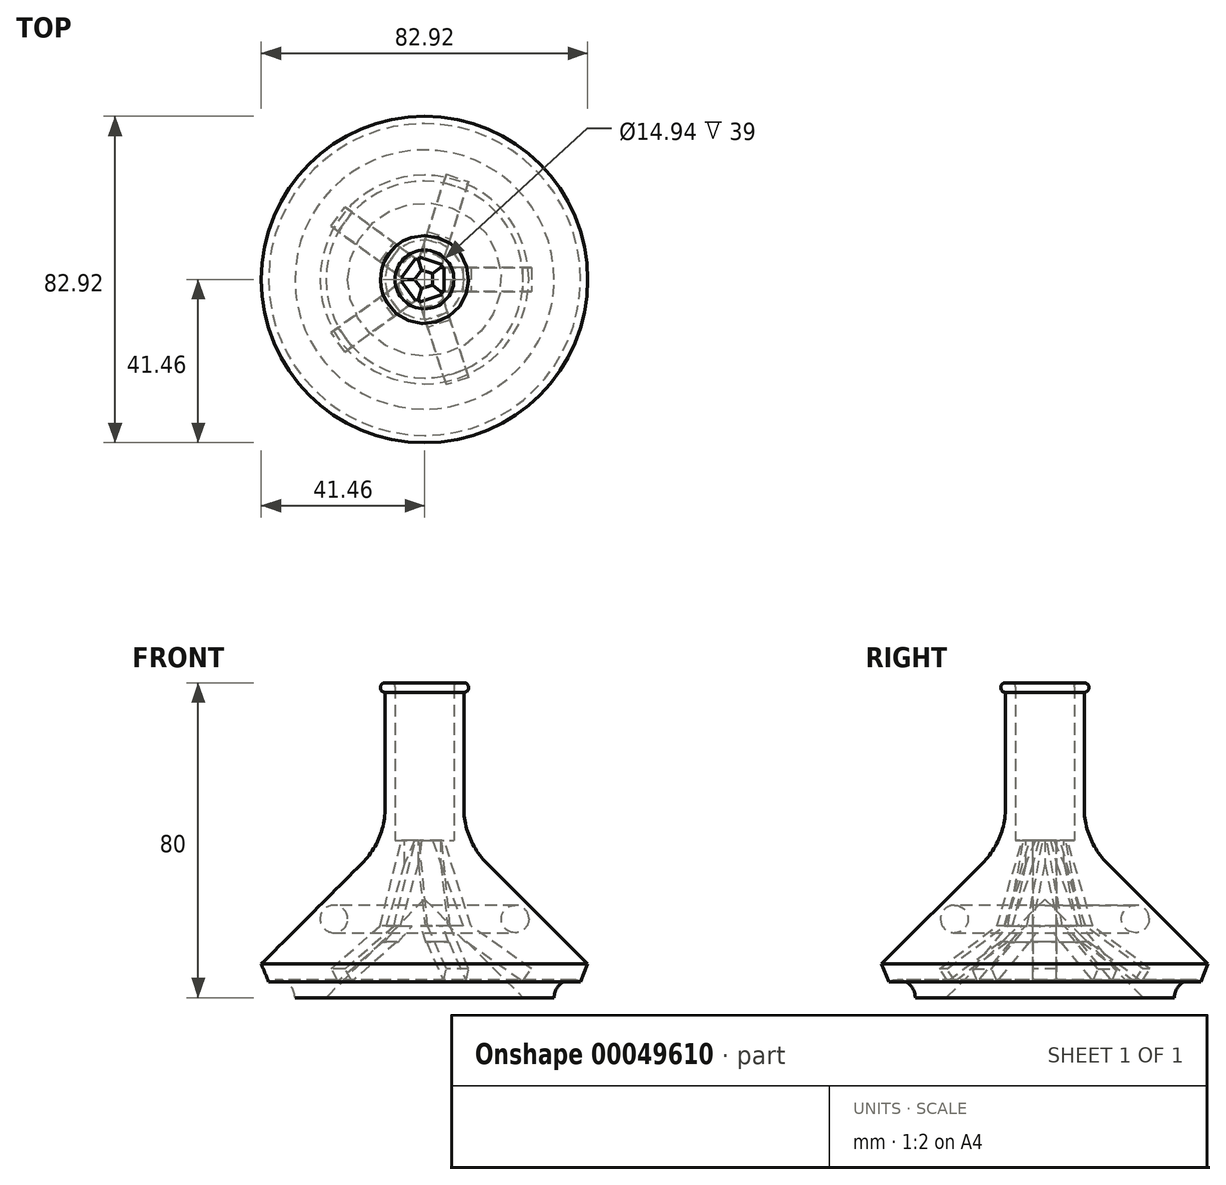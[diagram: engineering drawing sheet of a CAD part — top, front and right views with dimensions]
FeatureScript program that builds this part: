
annotation { "Feature Type Name" : "Feature", "Feature Type Description" : "" }
export const myFeature = defineFeature(function(context is Context, id is Id, definition is map)
    precondition{}
    {
        {
            var Q0;
            Q0=qCreatedBy(makeId("Front.planeOp"),FACE);
            var sketch = newSketch(context, id + "F0", { "sketchPlane" : qUnion([Q0])});
            skLineSegment(sketch, "E0", {"start": v(0, 0) * mm, "end": v(0, 80) * mm, "construction": true});
            skLineSegment(sketch, "E1", {"start": v(0, 80) * mm, "end": v(10, 80) * mm, "construction": true});
            skLineSegment(sketch, "E2", {"start": v(10, 80) * mm, "end": v(10, 40) * mm});
            skLineSegment(sketch, "E3", {"start": v(10, 40) * mm, "end": v(50, 0) * mm});
            skLineSegment(sketch, "E4", {"start": v(50, 0) * mm, "end": v(0, 0) * mm, "construction": true});
            skLineSegment(sketch, "E5", {"start": v(10, 80) * mm, "end": v(7.47, 80) * mm});
            skLineSegment(sketch, "E6", {"start": v(7.47, 80) * mm, "end": v(7.47, 40) * mm});
            skLineSegment(sketch, "E7", {"start": v(7.47, 40) * mm, "end": v(0, 40) * mm});
            skLineSegment(sketch, "E8", {"start": v(0, 40) * mm, "end": v(0, 25) * mm});
            skLineSegment(sketch, "E9", {"start": v(25, 0) * mm, "end": v(50, 0) * mm, "construction": true});
            skArc(sketch, "E10", {"start": v(42.08, 0) * mm, "mid": v(37.5, 4.58) * mm, "end": v(32.92, 0) * mm});
            skLineSegment(sketch, "E11", {"start": v(25, 0) * mm, "end": v(32.92, 0) * mm});
            skLineSegment(sketch, "E12", {"start": v(42.08, 0) * mm, "end": v(50, 0) * mm});
            skArc(sketch, "E13", {"start": v(10, 77.59) * mm, "mid": v(11.2, 78.8) * mm, "end": v(10, 80) * mm});
            skLineSegment(sketch, "E14", {"start": v(0, 25) * mm, "end": v(25, 0) * mm});
            skLineSegment(sketch, "E15", {"start": v(30, 20) * mm, "end": v(23, 20) * mm, "construction": true});
            skCircle(sketch, "E16", {"center": v(23, 20) * mm, "radius": 3.5 * mm});
            skSolve(sketch);
        }
        {
            var Q0;
            Q0=qSketchRegion(id+"F0",true);
            var Q1;
            Q1=sQuery(id+"F0.wireOp",EDGE,"E0");
            revolve(context, id + "F1", {"entities" : qUnion([Q0]), "axis" : qUnion([Q1]), "revolveType" : RevolveType.SYMMETRIC, "angle" : 72 * degree});
        }
        {
            var Q0;
            Q0=qCreatedBy(makeId("Front.planeOp"),FACE);
            var sketch = newSketch(context, id + "F2", { "sketchPlane" : qUnion([Q0])});
            skPoint(sketch, "E17.0", {"position": v(0, 40) * mm});
            skLineSegment(sketch, "E18", {"start": v(5.99, 44.01) * mm, "end": v(50, 0) * mm, "construction": true});
            skLineSegment(sketch, "E19", {"start": v(10, 80) * mm, "end": v(10, 40) * mm, "construction": true});
            skLineSegment(sketch, "E20", {"start": v(0, 40) * mm, "end": v(2, 40) * mm, "construction": true});
            skLineSegment(sketch, "E21", {"start": v(2, 40) * mm, "end": v(5, 40) * mm});
            skLineSegment(sketch, "E22", {"start": v(28, 22) * mm, "end": v(27.29, 21.3) * mm, "construction": true});
            skLineSegment(sketch, "E23", {"start": v(27.29, 21.3) * mm, "end": v(5, 40) * mm, "construction": true});
            skLineSegment(sketch, "E24", {"start": v(27.29, 21.3) * mm, "end": v(26, 19.77) * mm, "construction": true});
            skLineSegment(sketch, "E25", {"start": v(26, 19.77) * mm, "end": v(2, 40) * mm, "construction": true});
            skLineSegment(sketch, "E26", {"start": v(26.64, 20.53) * mm, "end": v(29.7, 17.96) * mm, "construction": true});
            skLineSegment(sketch, "E27", {"start": v(29.7, 17.96) * mm, "end": v(33.45, 16.55) * mm, "construction": true});
            skLineSegment(sketch, "E28", {"start": v(33.45, 16.55) * mm, "end": v(28, 22) * mm, "construction": true});
            skLineSegment(sketch, "E29", {"start": v(26, 19.77) * mm, "end": v(26, 0) * mm, "construction": true});
            skLineSegment(sketch, "E30", {"start": v(26, 0) * mm, "end": v(29.7, 0) * mm, "construction": true});
            skLineSegment(sketch, "E31", {"start": v(29.7, 0) * mm, "end": v(29.7, 17.96) * mm, "construction": true});
            skLineSegment(sketch, "E32", {"start": v(0.24, 24.76) * mm, "end": v(21.38, 3.62) * mm, "construction": true});
            skLineSegment(sketch, "E33", {"start": v(2, 40) * mm, "end": v(9.81, 18.19) * mm});
            skLineSegment(sketch, "E34", {"start": v(6.81, 18.19) * mm, "end": v(4.63, 18.19) * mm});
            skLineSegment(sketch, "E35", {"start": v(4.63, 18.19) * mm, "end": v(9.72, 13.1) * mm});
            skLineSegment(sketch, "E36", {"start": v(9.72, 13.1) * mm, "end": v(10.81, 14.19) * mm});
            skLineSegment(sketch, "E37", {"start": v(10.81, 14.19) * mm, "end": v(24.92, 4.18) * mm});
            skLineSegment(sketch, "E38", {"start": v(24.92, 4.18) * mm, "end": v(27.14, 7.3) * mm});
            skLineSegment(sketch, "E39", {"start": v(27.14, 7.3) * mm, "end": v(11.81, 18.19) * mm});
            skLineSegment(sketch, "E40", {"start": v(11.81, 18.19) * mm, "end": v(5, 40) * mm});
            skLineSegment(sketch, "E41", {"start": v(11.81, 18.19) * mm, "end": v(9.81, 18.19) * mm, "construction": true});
            skLineSegment(sketch, "E42", {"start": v(10.81, 18.19) * mm, "end": v(10.81, 14.19) * mm, "construction": true});
            skLineSegment(sketch, "E43", {"start": v(6.81, 18.19) * mm, "end": v(9.81, 18.19) * mm});
            skSolve(sketch);
        }
        {
            var Q0;
            Q0=qSketchRegion(id+"F2",true);
            extrude(context, id + "F3", {"entities" : qUnion([Q0]), "operationType" : NewBodyOperationType.REMOVE, "endBound" : BoundingType.SYMMETRIC, "oppositeDirection" : true, "depth" : 6 * mm});
        }
        {
            var Q0;
            Q0=makeQuery(id+"F1.opRevolve","SWEPT_BODY",BODY,{"disambiguationData":[OSD([sQuery(id+"F0.wireOp",EDGE,"E2"),sQuery(id+"F0.wireOp",EDGE,"E3"),sQuery(id+"F0.wireOp",EDGE,"E5"),sQuery(id+"F0.wireOp",EDGE,"E6"),sQuery(id+"F0.wireOp",EDGE,"E7"),sQuery(id+"F0.wireOp",EDGE,"93deaf08-34c0-4183-b7e3-c0240623c559"),sQuery(id+"F0.wireOp",EDGE,"E8"),sQuery(id+"F0.wireOp",EDGE,"E10"),sQuery(id+"F0.wireOp",EDGE,"E11"),sQuery(id+"F0.wireOp",EDGE,"E12")])]});
            var Q1;
            Q1=makeQuery(id+"F1.opRevolve","CAP_EDGE",EDGE,{"disambiguationData":[OSD([sQuery(id+"F0.wireOp",EDGE,"E8")])],"isStart":true});
            circularPattern(context, id + "F4", {"operationType" : NewBodyOperationType.ADD, "entities" : qUnion([Q0]), "axis" : qUnion([Q1]), "angle" : 72 * degree, "instanceCount" : 5});
        }
        {
            var Q0;
            {var subQ0=makeQuery(id+"F1.opRevolve","SWEPT_FACE",FACE,{"disambiguationData":[OSD([sQuery(id+"F0.wireOp",EDGE,"E5")])]});Q0=makeQuery(id+"F4.boolean.opBoolean","MERGE",FACE,{"derivedFrom":[subQ0,makeQuery(id+"F4.opPattern","COPY",FACE,{"derivedFrom":subQ0,"instanceName":"1"}),makeQuery(id+"F4.opPattern","COPY",FACE,{"derivedFrom":subQ0,"instanceName":"2"}),makeQuery(id+"F4.opPattern","COPY",FACE,{"derivedFrom":subQ0,"instanceName":"3"}),makeQuery(id+"F4.opPattern","COPY",FACE,{"derivedFrom":subQ0,"instanceName":"4"}),makeQuery(id+"F4.opPattern","COPY",FACE,{"derivedFrom":subQ0,"instanceName":"5"}),makeQuery(id+"F4.opPattern","COPY",FACE,{"derivedFrom":subQ0,"instanceName":"6"}),makeQuery(id+"F4.opPattern","COPY",FACE,{"derivedFrom":subQ0,"instanceName":"7"}),makeQuery(id+"F4.opPattern","COPY",FACE,{"derivedFrom":subQ0,"instanceName":"8"}),makeQuery(id+"F4.opPattern","COPY",FACE,{"derivedFrom":subQ0,"instanceName":"9"})]});}
            fillet(context, id + "F5", {"entities" : qUnion([Q0]), "radius" : 1 * mm, "tangentPropagation" : true, "allowEdgeOverflow" : false});
        }
        {
            var Q0;
            {var subQ0=makeQuery(id+"F1.opRevolve","SWEPT_EDGE",EDGE,{"disambiguationData":[OSD([sQuery(id+"F0.wireOp",EDGE,"E3"),sQuery(id+"F0.wireOp",EDGE,"E12")])]});Q0=makeQuery(id+"F4.boolean.opBoolean","MERGE",EDGE,{"derivedFrom":[subQ0,makeQuery(id+"F4.opPattern","COPY",EDGE,{"derivedFrom":subQ0,"instanceName":"1"}),makeQuery(id+"F4.opPattern","COPY",EDGE,{"derivedFrom":subQ0,"instanceName":"2"}),makeQuery(id+"F4.opPattern","COPY",EDGE,{"derivedFrom":subQ0,"instanceName":"3"}),makeQuery(id+"F4.opPattern","COPY",EDGE,{"derivedFrom":subQ0,"instanceName":"4"}),makeQuery(id+"F4.opPattern","COPY",EDGE,{"derivedFrom":subQ0,"instanceName":"5"}),makeQuery(id+"F4.opPattern","COPY",EDGE,{"derivedFrom":subQ0,"instanceName":"6"}),makeQuery(id+"F4.opPattern","COPY",EDGE,{"derivedFrom":subQ0,"instanceName":"7"}),makeQuery(id+"F4.opPattern","COPY",EDGE,{"derivedFrom":subQ0,"instanceName":"8"}),makeQuery(id+"F4.opPattern","COPY",EDGE,{"derivedFrom":subQ0,"instanceName":"9"})]});}
            chamfer(context, id + "F6", {"entities" : qUnion([Q0]), "width" : 5 * mm, "tangentPropagation" : true});
        }
        {
            var Q0;
            {var subQ0=makeQuery(id+"F1.opRevolve","SWEPT_EDGE",EDGE,{"disambiguationData":[OSD([sQuery(id+"F0.wireOp",EDGE,"E2"),sQuery(id+"F0.wireOp",EDGE,"E3")])]});Q0=makeQuery(id+"F4.boolean.opBoolean","MERGE",EDGE,{"derivedFrom":[subQ0,makeQuery(id+"F4.opPattern","COPY",EDGE,{"derivedFrom":subQ0,"instanceName":"1"}),makeQuery(id+"F4.opPattern","COPY",EDGE,{"derivedFrom":subQ0,"instanceName":"2"}),makeQuery(id+"F4.opPattern","COPY",EDGE,{"derivedFrom":subQ0,"instanceName":"3"}),makeQuery(id+"F4.opPattern","COPY",EDGE,{"derivedFrom":subQ0,"instanceName":"4"}),makeQuery(id+"F4.opPattern","COPY",EDGE,{"derivedFrom":subQ0,"instanceName":"5"}),makeQuery(id+"F4.opPattern","COPY",EDGE,{"derivedFrom":subQ0,"instanceName":"6"}),makeQuery(id+"F4.opPattern","COPY",EDGE,{"derivedFrom":subQ0,"instanceName":"7"}),makeQuery(id+"F4.opPattern","COPY",EDGE,{"derivedFrom":subQ0,"instanceName":"8"}),makeQuery(id+"F4.opPattern","COPY",EDGE,{"derivedFrom":subQ0,"instanceName":"9"})]});}
            fillet(context, id + "F7", {"entities" : qUnion([Q0]), "radius" : 20 * mm, "tangentPropagation" : true, "allowEdgeOverflow" : false});
        }
    });
